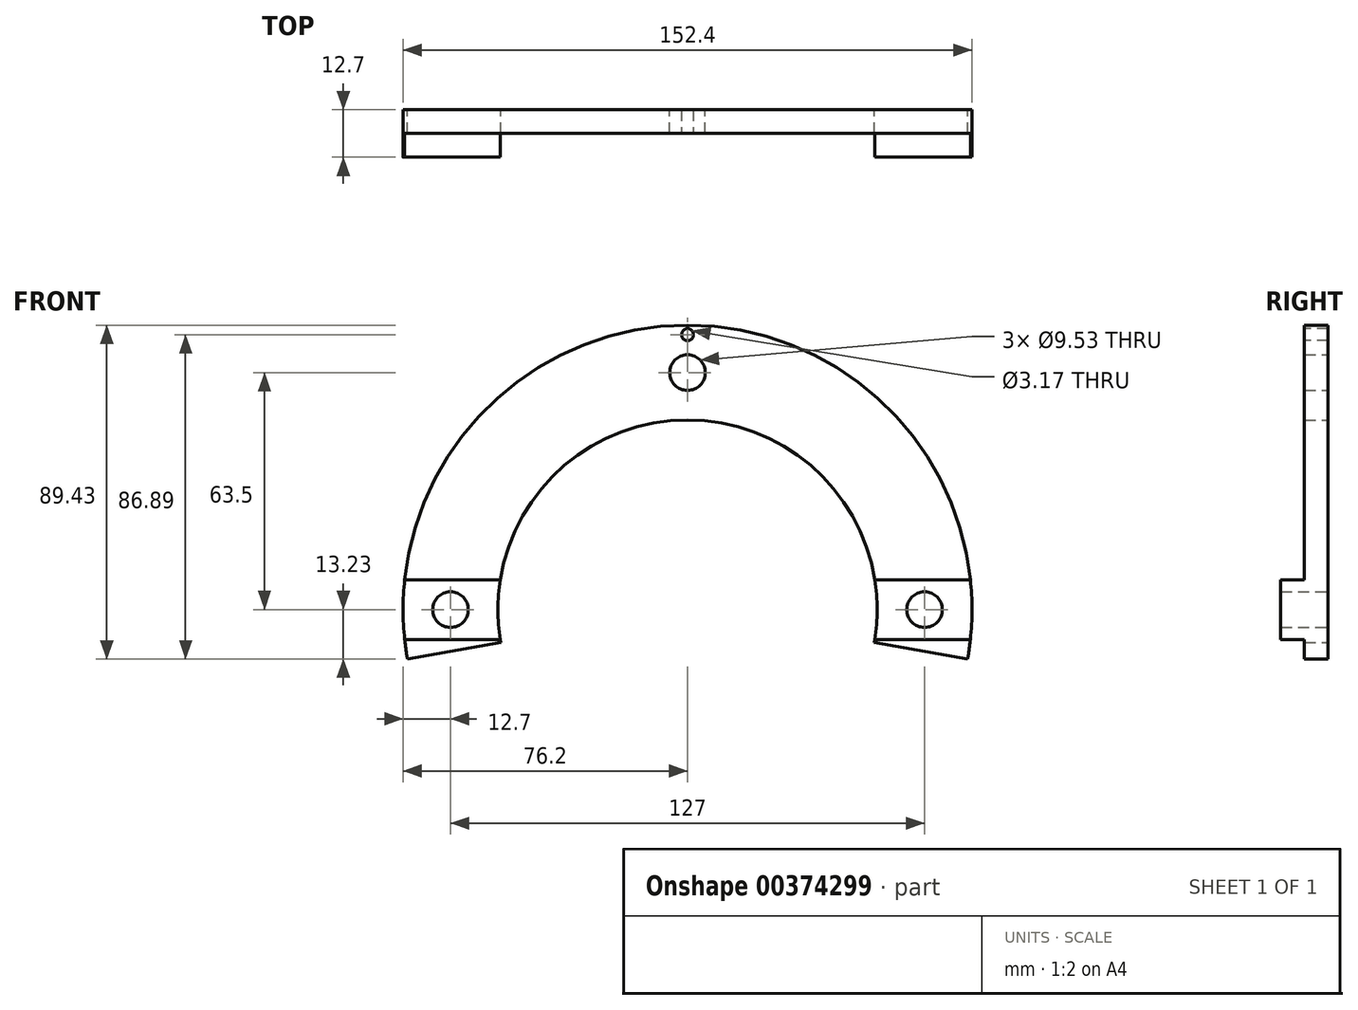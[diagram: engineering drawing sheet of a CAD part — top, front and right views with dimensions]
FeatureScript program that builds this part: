
annotation { "Feature Type Name" : "Feature", "Feature Type Description" : "" }
export const myFeature = defineFeature(function(context is Context, id is Id, definition is map)
    precondition{}
    {
        {
            var Q0;
            Q0=qCreatedBy(makeId("Front.planeOp"),FACE);
            var sketch = newSketch(context, id + "F0", { "sketchPlane" : qUnion([Q0])});
            skArc(sketch, "E0", {"start": v(75.04, -13.23) * mm, "mid": v(0, 76.2) * mm, "end": v(-75.04, -13.23) * mm});
            skCircle(sketch, "E1", {"center": v(-63.5, 0) * mm, "radius": 4.76 * mm});
            skCircle(sketch, "E2", {"center": v(63.5, 0) * mm, "radius": 4.76 * mm});
            skCircle(sketch, "E3", {"center": v(0, 63.5) * mm, "radius": 4.76 * mm});
            skArc(sketch, "E4", {"start": v(62.54, -11.03) * mm, "mid": v(0, 63.5) * mm, "end": v(-62.54, -11.03) * mm, "construction": true});
            skArc(sketch, "E5", {"start": v(50.03, -8.82) * mm, "mid": v(0, 50.8) * mm, "end": v(-50.03, -8.82) * mm});
            skLineSegment(sketch, "E6", {"start": v(-50.03, -8.82) * mm, "end": v(-75.04, -13.23) * mm});
            skLineSegment(sketch, "E7", {"start": v(50.03, -8.82) * mm, "end": v(75.04, -13.23) * mm});
            skCircle(sketch, "E8", {"center": v(0, 53.34) * mm, "radius": 1.59 * mm, "construction": true});
            skSolve(sketch);
        }
        {
            var Q0;
            Q0=makeQuery(id+"F0.imprint","IMPRINT",FACE,{"disambiguationData":[TD([[makeQuery(id+"F0.imprint","IMPRINT",EDGE,{"derivedFrom":sQuery(id+"F0.wireOp",EDGE,"E0")}),1.0]])]});
            extrude(context, id + "F1", {"entities" : qUnion([Q0]), "depth" : 6.35 * mm});
        }
        {
            var Q0;
            Q0=makeQuery(id+"F1.opExtrude","CAP_FACE",FACE,{"disambiguationData":[OSD([sQuery(id+"F0.wireOp",EDGE,"E0"),sQuery(id+"F0.wireOp",EDGE,"E1"),sQuery(id+"F0.wireOp",EDGE,"E2"),sQuery(id+"F0.wireOp",EDGE,"E3"),sQuery(id+"F0.wireOp",EDGE,"E5"),sQuery(id+"F0.wireOp",EDGE,"E6"),sQuery(id+"F0.wireOp",EDGE,"E7")])],"isStart":false});
            var sketch = newSketch(context, id + "F2", { "sketchPlane" : qUnion([Q0])});
            skLineSegment(sketch, "E9.bottom", {"start": v(-75.78, 8) * mm, "end": v(-50.17, 8) * mm});
            skLineSegment(sketch, "E9.top", {"start": v(-75.78, -8) * mm, "end": v(-50.17, -8) * mm});
            skArc(sketch, "E10.0", {"start": v(75.78, -8) * mm, "mid": v(76.2, 0) * mm, "end": v(75.78, 8) * mm});
            skArc(sketch, "E11.0", {"start": v(50.17, -8) * mm, "mid": v(50.8, 0) * mm, "end": v(50.17, 8) * mm});
            skLineSegment(sketch, "E12.trimOffspring", {"start": v(50.17, -8) * mm, "end": v(75.78, -8) * mm});
            skLineSegment(sketch, "E13.trimOffspring", {"start": v(50.17, 8) * mm, "end": v(75.78, 8) * mm});
            skArc(sketch, "E14.trimOffspring", {"start": v(-75.78, 8) * mm, "mid": v(-76.2, 0) * mm, "end": v(-75.78, -8) * mm});
            skArc(sketch, "E15.trimOffspring", {"start": v(-50.17, 8) * mm, "mid": v(-50.8, 0) * mm, "end": v(-50.17, -8) * mm});
            skPoint(sketch, "E16.orphan", {"position": v(-75.04, -13.23) * mm});
            skPoint(sketch, "E17.orphan", {"position": v(-50.03, -8.82) * mm});
            skPoint(sketch, "E18.orphan", {"position": v(50.03, -8.82) * mm});
            skPoint(sketch, "E19.orphan", {"position": v(75.04, -13.23) * mm});
            skCircle(sketch, "E20.0", {"center": v(-63.5, 0) * mm, "radius": 4.76 * mm});
            skCircle(sketch, "E21.0", {"center": v(63.5, 0) * mm, "radius": 4.76 * mm});
            skSolve(sketch);
        }
        {
            var Q0;
            Q0=makeQuery(id+"F2.imprint","IMPRINT",FACE,{"disambiguationData":[TD([[makeQuery(id+"F2.imprint","IMPRINT",EDGE,{"derivedFrom":sQuery(id+"F2.wireOp",EDGE,"E9.bottom")}),-1.0]])]});
            var Q1;
            Q1=makeQuery(id+"F2.imprint","IMPRINT",FACE,{"disambiguationData":[TD([[makeQuery(id+"F2.imprint","IMPRINT",EDGE,{"derivedFrom":sQuery(id+"F2.wireOp",EDGE,"E10.0")}),1.0]])]});
            extrude(context, id + "F3", {"entities" : qUnion([Q0, Q1]), "operationType" : NewBodyOperationType.ADD, "depth" : 6.35 * mm});
        }
        {
            var Q0;
            {var subQ0=sQuery(id+"F0.wireOp",EDGE,"E5");var subQ1=sQuery(id+"F0.wireOp",EDGE,"E3");var subQ2=sQuery(id+"F0.wireOp",EDGE,"E0");Q0=makeQuery(id+"F3.boolean.opBoolean","SPLIT",FACE,{"disambiguationData":[TD([makeQuery(id+"F1.opExtrude","SWEPT_FACE",FACE,{"disambiguationData":[OSD([subQ1])]})])],"derivedFrom":makeQuery(id+"F1.opExtrude","CAP_FACE",FACE,{"disambiguationData":[OSD([subQ2,sQuery(id+"F0.wireOp",EDGE,"E1"),sQuery(id+"F0.wireOp",EDGE,"E2"),subQ1,subQ0,sQuery(id+"F0.wireOp",EDGE,"E6"),sQuery(id+"F0.wireOp",EDGE,"E7")])],"isStart":false})});}
            var sketch = newSketch(context, id + "F4", { "sketchPlane" : qUnion([Q0])});
            skCircle(sketch, "E22", {"center": v(0, 73.66) * mm, "radius": 1.59 * mm});
            skCircle(sketch, "E23.0", {"center": v(0, 63.5) * mm, "radius": 4.76 * mm});
            skSolve(sketch);
        }
        {
            var Q0;
            Q0=makeQuery(id+"F4.imprint","IMPRINT",FACE,{"disambiguationData":[TD([[makeQuery(id+"F4.imprint","IMPRINT",EDGE,{"derivedFrom":sQuery(id+"F4.wireOp",EDGE,"E22")}),1.0]])]});
            extrude(context, id + "F5", {"entities" : qUnion([Q0]), "operationType" : NewBodyOperationType.REMOVE, "oppositeDirection" : true, "depth" : 12.7 * mm});
        }
    });
